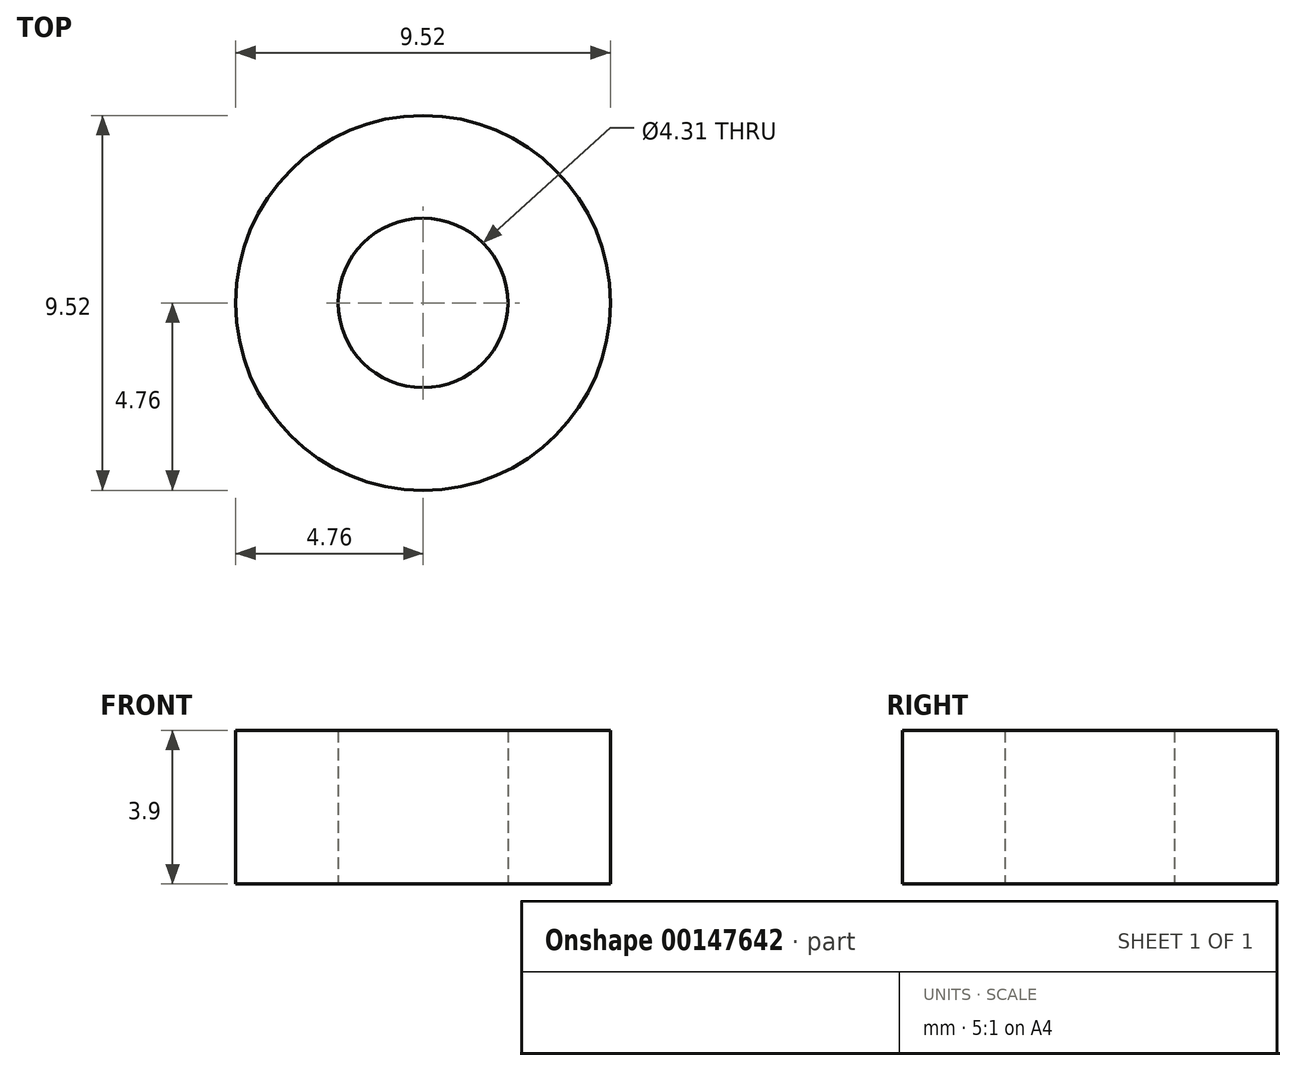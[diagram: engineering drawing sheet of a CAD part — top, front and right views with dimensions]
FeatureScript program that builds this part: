
annotation { "Feature Type Name" : "Feature", "Feature Type Description" : "" }
export const myFeature = defineFeature(function(context is Context, id is Id, definition is map)
    precondition{}
    {
        {
            var Q0;
            Q0=qCreatedBy(makeId("Top.planeOp"),FACE);
            var sketch = newSketch(context, id + "F0", { "sketchPlane" : qUnion([Q0])});
            skCircle(sketch, "E0", {"center": v(0, 0) * mm, "radius": 4.76 * mm});
            skCircle(sketch, "E1", {"center": v(0, 0) * mm, "radius": 2.15 * mm});
            skSolve(sketch);
        }
        {
            var Q0;
            Q0=qSketchRegion(id+"F0",true);
            extrude(context, id + "F1", {"entities" : qUnion([Q0]), "depth" : 3.9 * mm});
        }
    });
